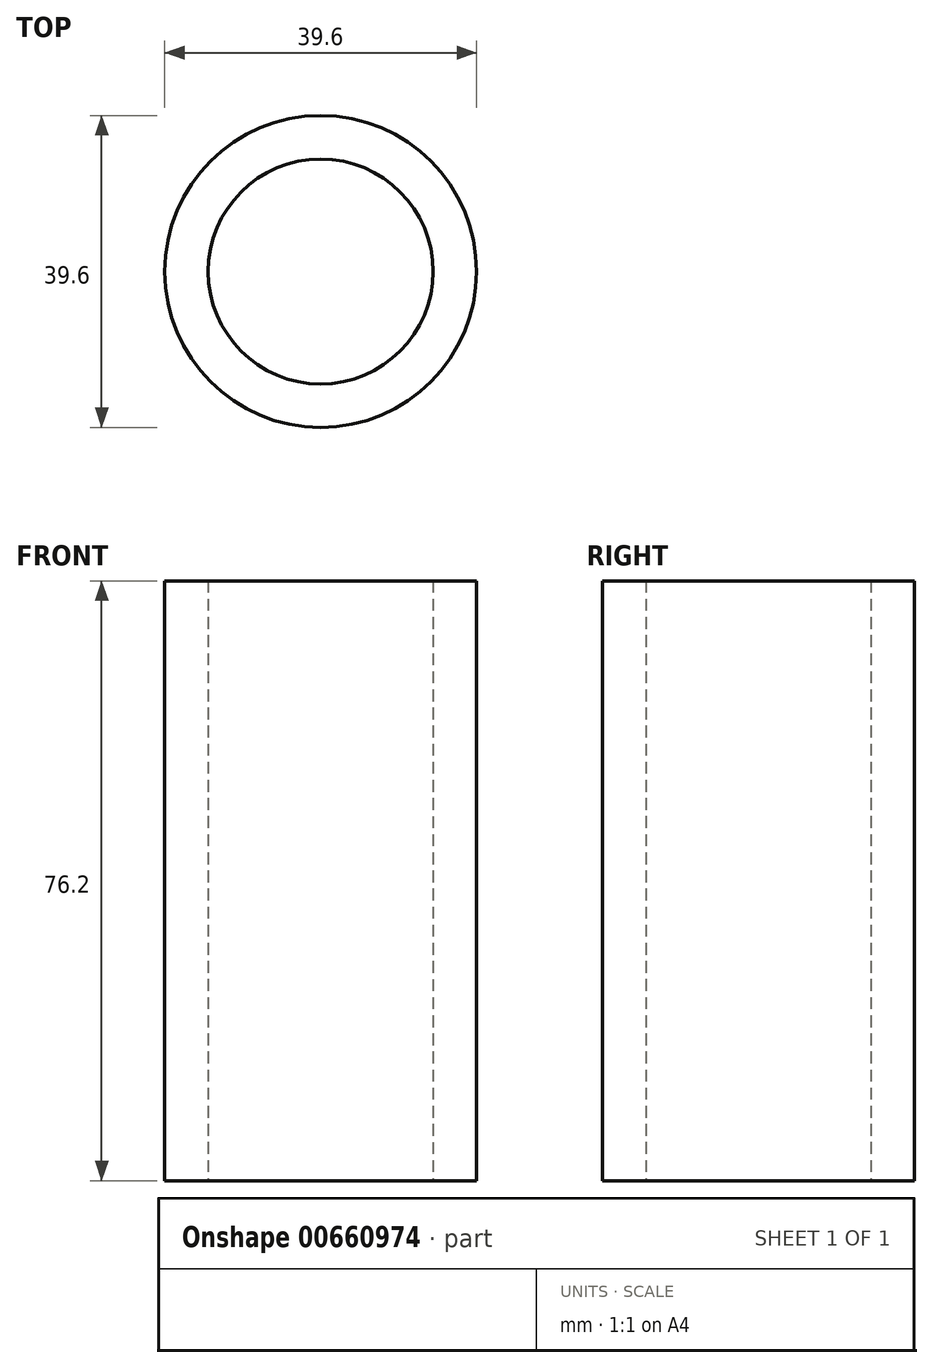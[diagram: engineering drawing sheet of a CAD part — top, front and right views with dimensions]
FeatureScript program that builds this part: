
annotation { "Feature Type Name" : "Feature", "Feature Type Description" : "" }
export const myFeature = defineFeature(function(context is Context, id is Id, definition is map)
    precondition{}
    {
        {
            var Q0;
            Q0=qCreatedBy(makeId("Top.planeOp"),FACE);
            var sketch = newSketch(context, id + "F0", { "sketchPlane" : qUnion([Q0])});
            skCircle(sketch, "E0", {"center": v(0, 0) * mm, "radius": 14.29 * mm});
            skCircle(sketch, "E1.0", {"center": v(0, 0) * mm, "radius": 17.46 * mm});
            skCircle(sketch, "E2", {"center": v(0, 0) * mm, "radius": 12.32 * mm});
            skCircle(sketch, "E3", {"center": v(0, 0) * mm, "radius": 10.16 * mm});
            skCircle(sketch, "E4", {"center": v(0, 0) * mm, "radius": 19.8 * mm});
            skSolve(sketch);
        }
        {
            var Q0;
            Q0=makeQuery(id+"F0.imprint","IMPRINT",FACE,{"disambiguationData":[TD([[makeQuery(id+"F0.imprint","IMPRINT",EDGE,{"derivedFrom":sQuery(id+"F0.wireOp",EDGE,"E1.0")}),-1.0]])]});
            var Q1;
            Q1=makeQuery(id+"F0.imprint","IMPRINT",FACE,{"disambiguationData":[TD([[makeQuery(id+"F0.imprint","IMPRINT",EDGE,{"derivedFrom":sQuery(id+"F0.wireOp",EDGE,"E0")}),-1.0]])]});
            extrude(context, id + "F1", {"entities" : qUnion([Q0, Q1]), "depth" : 76.2 * mm, "offsetDistance" : 25.4 * mm});
        }
    });
